# Revit family: Shower-Floor_Drain-KOHLER-Hidden-K-33622T
name_source: partatom
category: Plumbing Fixtures
units: mm (PartAtom-declared; Revit-internal decimal feet)

## family parameters
Cut with Voids When Loaded = No
Host = Face
OmniClass Number = 23.39.29.11
OmniClass Title = Waste Water Drains
Part Type = Normal
Room Calculation Point = No
Round Connector Dimension = Use Diameter
Shared = No

## types (3) — shared parameters
ADA Compliant = No
Assembly Code = D2010700
CW Connection = No
Cold Water Inlet = Cold Water Inlet
Date Modified = 07/12/2024
Default Elevation = 0"
Description = Floor Drain (E) 600 X 28MM
Drain Included = No
Flow Rate = 0 GPM
HW Connection = No
Height = 2 3/8"
Hot Water Inlet = Hot Water Inlet
Length = 1 1/8"
Manufacturer = Kohler Co.
Master Format 2014 = 22 42 23
Master Format 2014 Name = Residential Showers
Material = Premium Metal Construction
Pressure = 0.00 psi
Product Name = Hidden
URL = http://www.kohler.com.cn
Vent Connection = No
Waste Connection = Yes
Waste Water Outlet = Waste Water Outlet
WaterSense Certified = No
Width = 23 5/8"

## per-type parameters (varying)
| type | Finish | Model | Type |
| BS-Brushed Stainless | Kohler-Metal-BS-Brushed_Stainless | K-33622T-BS | 2 |
| 2MB-Vibrant Brushed Moderne Brass | Kohler-Metal-2MB-Vibrant_Brushed_Moderne_Brass | K-33622T-2MB | 1 |
| CG2-Cool Dark Gray | KOHLER-Metal-CG2-Cool_Dark_Gray | K-33622T-CG2 | 3 |

## geometry (parser evidence)
native form markers: Sweep x5
no freeform markers — native parametric forms only
